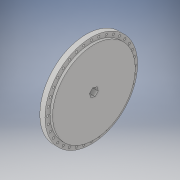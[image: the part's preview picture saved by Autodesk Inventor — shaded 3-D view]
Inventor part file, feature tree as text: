
AUTODESK INVENTOR PART (.ipt)
format: ipt  version: 2018 (Build 220112000, 112)  size: 167,424 bytes
history: native  units: in
note: dims shown in document units (in); Inventor stores cm internally (conversion verified against a paired STEP export)
features: extrude x3, sketch x3, pattern_circular x1, projected_geometry x1
ambient origin geometry x8: Origin, YZ Plane, XZ Plane, XY Plane, X Axis, Y Axis, Z Axis, Center Point
bodies: Solid1 (feature_tree)
feature tree (8):
  extrude  "Extrusion1"  Depth=0.38in
  extrude  "Extrusion2"  Depth=0.25in
  extrude  "Extrusion3"  Depth=0.25in
  pattern_circular  "Circular Pattern1"  [2 undecoded]
  sketch  "Sketch1"  dims[d0=4.5in d1=0.38in]
  sketch  "Sketch2"  dims[d2=0.25in d3=0.0in d4=4.015in]
  sketch  "Sketch3"  dims[d5=0.125in d6=0.0in d7=0.11in d8=2.125in d9=0.25in d10=0.0in d11=14.1732in d12=360.0deg]
  projected_geometry  "Projected Loop1"
note: 2 required parameter values undecoded (feature->parameter linkage not recoverable at this tier; creation-order binding heuristic only, values carry confidence <= 0.55)
